# Revit family: Layouts-Teknion-Byward_13_Blended_Solutions-R2019
name_source: partatom
category: Furniture Systems
units: mm (PartAtom-declared; Revit-internal decimal feet)

## family parameters
Always vertical = Yes
Cut with Voids When Loaded = No
OmniClass Number = 23.40.70.14.64.21
OmniClass Title = Systems Furniture
Part Type = Normal
Room Calculation Point = No
Round Connector Dimension = Use Diameter
Shared = Yes
Work Plane-Based = No

## types (1)
- Byward 13
    Assembly Code = E2020200
    Description = 6'-0" x 10'-6" Overall
    Manufacturer = Teknion
    Manufacturer Fax = 416.661.4586
    Model = Bywards Layout 13 Blended Solutions
    Product Line = Bywards
    Product Page URL = https://www.teknionplanningtool.com
    Series = Bywards
    Sustainability Data = https://www.teknion.com
    URL = www.teknion.com
    Unit Weight URL = http://www.teknion.com
    Warranty = http://www.teknion.com

## geometry (parser evidence)
native form markers: Blend x17, Sweep x21
no freeform markers — native parametric forms only
